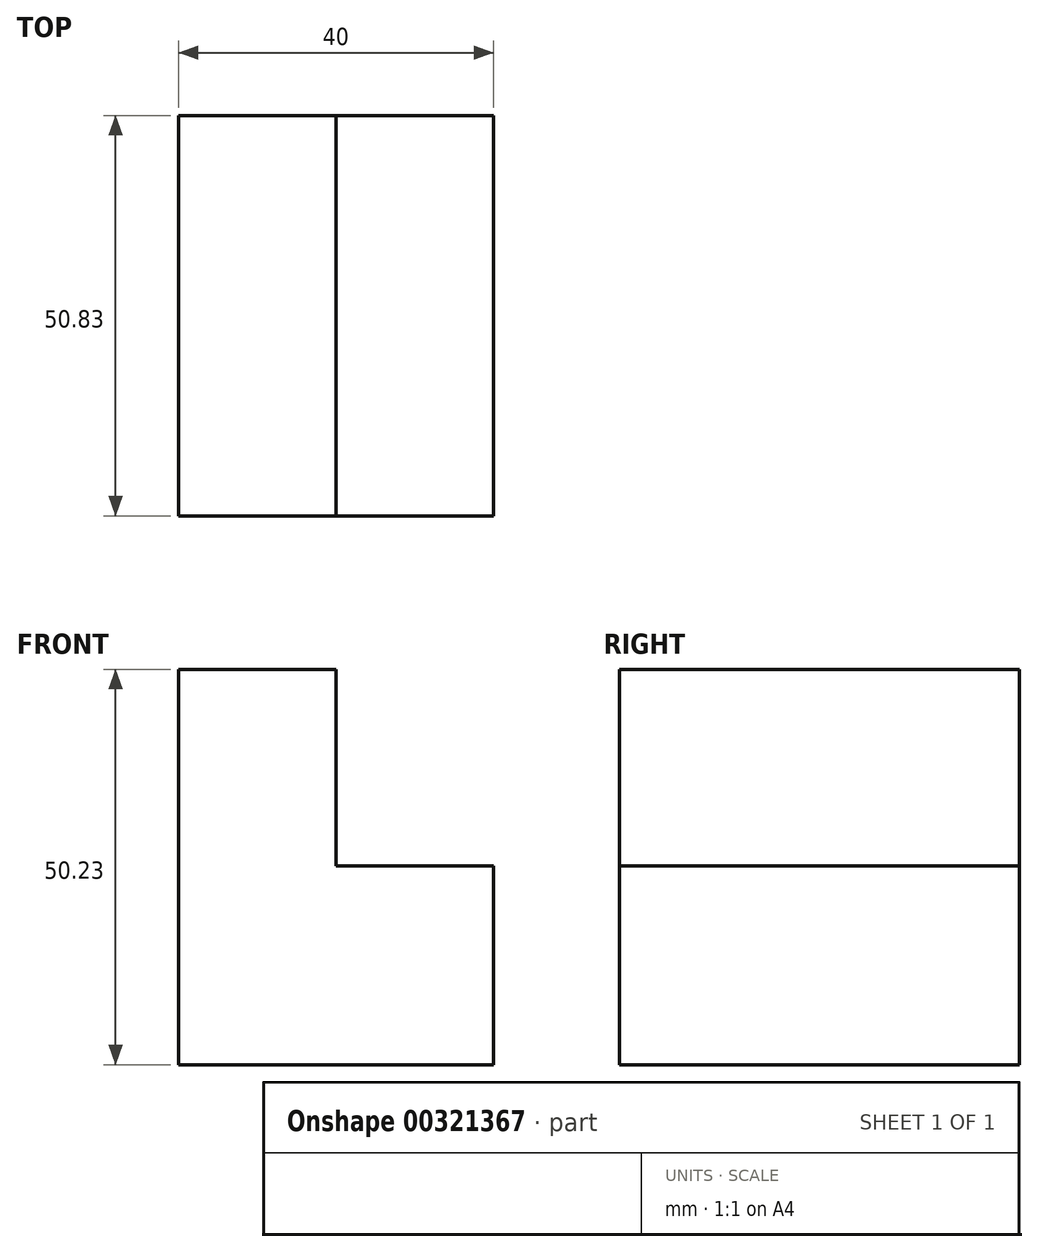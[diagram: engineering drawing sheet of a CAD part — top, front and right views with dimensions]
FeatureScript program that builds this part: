
annotation { "Feature Type Name" : "Feature", "Feature Type Description" : "" }
export const myFeature = defineFeature(function(context is Context, id is Id, definition is map)
    precondition{}
    {
        {
            var Q0;
            Q0=qCreatedBy(makeId("Right.planeOp"),FACE);
            var sketch = newSketch(context, id + "F0", { "sketchPlane" : qUnion([Q0])});
            skLineSegment(sketch, "E0.bottom", {"start": v(0, 0) * mm, "end": v(-50.83, 0) * mm});
            skLineSegment(sketch, "E0.top", {"start": v(0, 50.23) * mm, "end": v(-50.83, 50.23) * mm});
            skLineSegment(sketch, "E0.left", {"start": v(0, 0) * mm, "end": v(0, 50.23) * mm});
            skLineSegment(sketch, "E0.right", {"start": v(-50.83, 0) * mm, "end": v(-50.83, 50.23) * mm});
            skSolve(sketch);
        }
        {
            var Q0;
            Q0 = qSketchRegion(id + "F0", true);
            extrude(context, id + "F1", {"entities" : qUnion([Q0]), "depth" : 20 * mm});
        }
        {
            var Q0;
            Q0=qCreatedBy(makeId("Right.planeOp"),FACE);
            var sketch = newSketch(context, id + "F2", { "sketchPlane" : qUnion([Q0])});
            skLineSegment(sketch, "E1.bottom", {"start": v(0, 0) * mm, "end": v(-50.83, 0) * mm});
            skLineSegment(sketch, "E1.top", {"start": v(0, 25.27) * mm, "end": v(-50.83, 25.27) * mm});
            skLineSegment(sketch, "E1.left", {"start": v(0, 0) * mm, "end": v(0, 25.27) * mm});
            skLineSegment(sketch, "E1.right", {"start": v(-50.83, 0) * mm, "end": v(-50.83, 25.27) * mm});
            skSolve(sketch);
        }
        {
            var Q0;
            Q0 = qSketchRegion(id + "F2", true);
            extrude(context, id + "F3", {"entities" : qUnion([Q0]), "operationType" : NewBodyOperationType.ADD, "depth" : 40 * mm});
        }
    });
